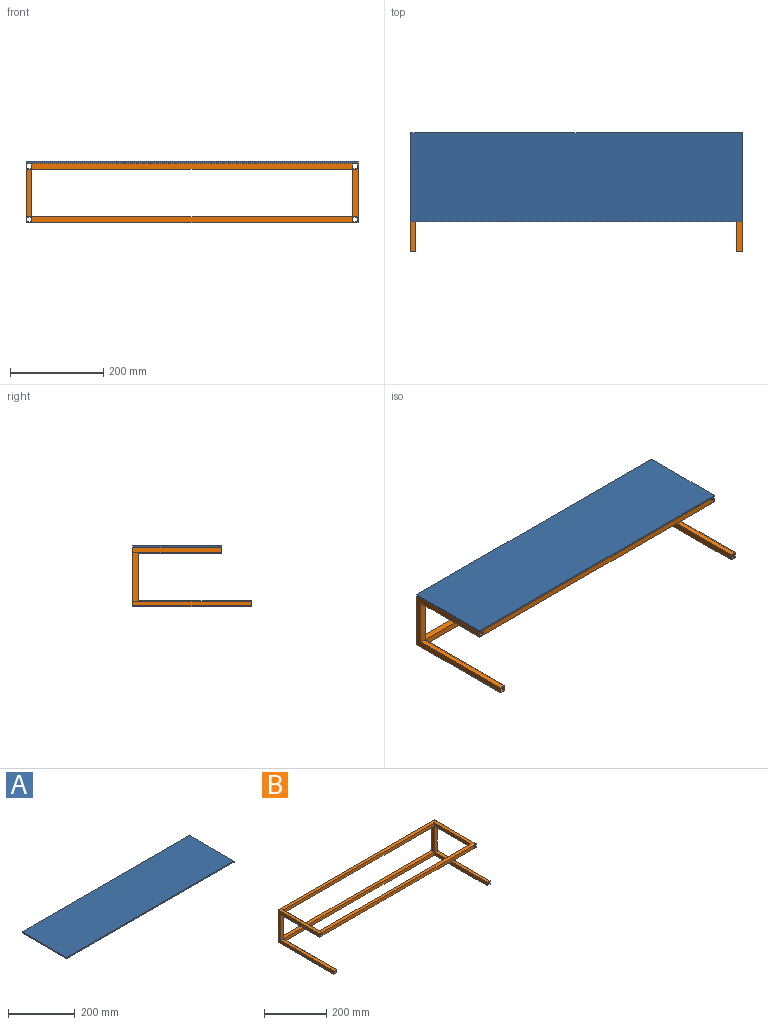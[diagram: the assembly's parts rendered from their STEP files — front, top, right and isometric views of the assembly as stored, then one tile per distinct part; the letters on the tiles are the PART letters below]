
ASSEMBLY  parts=2 mates=1
PART A: 6 faces, bbox 711.2x190.5x4.1 mm
  f0: plane 190.5x4.06mm, normal (-1,0,0), area 774.2mm2, adj f1,f3,f4,f5
  f1: plane 711.2x4.06mm, normal (0,-1,0), area 2890.3mm2, adj f0,f2,f4,f5
  f2: plane 190.5x4.06mm, normal (1,0,0), area 774.2mm2, adj f1,f3,f4,f5
  f3: plane 711.2x4.06mm, normal (0,1,0), area 2890.3mm2, adj f0,f2,f4,f5
  f4: plane 711.2x190.5mm, normal (0,0,1), area 135483.6mm2, adj f0,f1,f2,f3
  f5: plane 711.2x190.5mm, normal (0,0,-1), area 135483.6mm2, adj f0,f1,f2,f3
PART B: 40 faces, bbox 711.2x254x127 mm
  f0: plane 711.2x127mm, normal (0,1,0), area 20232.2mm2, adj f6,f7,f10,f11,f15,f17,f18,f22
  f1: plane 12.7x12.7mm, normal (0,-1,0), area 58.1mm2, adj f11,f12,f16,f17,f36,f37,f38,f39
  f2: plane 711.2x12.7mm, normal (0,-1,0), area 8825.8mm2, adj f11,f15,f18,f20,f28,f29,f30,f31
  f3: plane 12.7x12.7mm, normal (0,-1,0), area 58.1mm2, adj f9,f14,f15,f17,f24,f25,f26,f27
  f4: plane 165.1x12.7mm, normal (1,0,0), area 2096.8mm2, adj f18,f20,f21,f23
  f5: plane 165.1x12.7mm, normal (-1,0,0), area 2096.8mm2, adj f18,f20,f21,f23
  f6: plane 101.6x12.7mm, normal (1,0,0), area 1290.3mm2, adj f0,f8,f10,f22
  f7: plane 101.6x12.7mm, normal (-1,0,0), area 1290.3mm2, adj f0,f10,f19,f22
  f8: plane 101.6x12.7mm, normal (0,-1,0), area 1290.3mm2, adj f6,f11,f16,f20
  f9: plane 241.3x12.7mm, normal (0,0,1), area 3064.5mm2, adj f3,f14,f15,f19
  f10: plane 685.8x12.7mm, normal (0,0,1), area 8709.7mm2, adj f0,f6,f7,f13
  f11: plane 254x127mm, normal (-1,0,0), area 6935.5mm2, adj f0,f1,f2,f8,f16,f17,f18,f20
  f12: plane 241.3x12.7mm, normal (1,0,0), area 3064.5mm2, adj f1,f13,f16,f17
  f13: plane 685.8x12.7mm, normal (0,-1,0), area 8709.7mm2, adj f10,f12,f14,f17
  f14: plane 241.3x12.7mm, normal (-1,0,0), area 3064.5mm2, adj f3,f9,f13,f17
  f15: plane 254x127mm, normal (1,0,0), area 6935.5mm2, adj f0,f2,f3,f9,f17,f18,f19,f20
  f16: plane 241.3x12.7mm, normal (0,0,1), area 3064.5mm2, adj f1,f8,f11,f12
  f17: plane 711.2x254mm, normal (0,0,-1), area 15161.3mm2, adj f0,f1,f3,f11,f12,f13,f14,f15
  f18: plane 711.2x190.5mm, normal (0,0,1), area 22258mm2, adj f0,f2,f4,f5,f11,f15,f21,f23
  f19: plane 101.6x12.7mm, normal (0,-1,0), area 1290.3mm2, adj f7,f9,f15,f20
  f20: plane 711.2x177.8mm, normal (0,0,-1), area 13225.8mm2, adj f2,f4,f5,f8,f11,f15,f19,f23
  f21: plane 685.8x12.7mm, normal (0,-1,0), area 8709.7mm2, adj f4,f5,f18,f22
  f22: plane 685.8x12.7mm, normal (0,0,-1), area 8709.7mm2, adj f0,f6,f7,f21
  f23: plane 685.8x12.7mm, normal (0,1,0), area 8709.7mm2, adj f4,f5,f18,f20
  f24: plane 254x10.16mm, normal (0,0,-1), area 2580.6mm2, adj f0,f3,f25,f27
  f25: plane 254x10.16mm, normal (1,0,0), area 2580.6mm2, adj f0,f3,f24,f26
  f26: plane 254x10.16mm, normal (0,0,1), area 2580.6mm2, adj f0,f3,f25,f27
  f27: plane 254x10.16mm, normal (-1,0,0), area 2580.6mm2, adj f0,f3,f24,f26
  f28: plane 190.5x10.16mm, normal (0,0,-1), area 1935.5mm2, adj f0,f2,f29,f31
  f29: plane 190.5x10.16mm, normal (1,0,0), area 1935.5mm2, adj f0,f2,f28,f30
  f30: plane 190.5x10.16mm, normal (0,0,1), area 1935.5mm2, adj f0,f2,f29,f31
  f31: plane 190.5x10.16mm, normal (-1,0,0), area 1935.5mm2, adj f0,f2,f28,f30
  f32: plane 190.5x10.16mm, normal (-1,0,0), area 1935.5mm2, adj f0,f2,f33,f35
  f33: plane 190.5x10.16mm, normal (0,0,-1), area 1935.5mm2, adj f0,f2,f32,f34
  f34: plane 190.5x10.16mm, normal (1,0,0), area 1935.5mm2, adj f0,f2,f33,f35
  f35: plane 190.5x10.16mm, normal (0,0,1), area 1935.5mm2, adj f0,f2,f32,f34
  f36: plane 254x10.16mm, normal (0,0,-1), area 2580.6mm2, adj f0,f1,f37,f39
  f37: plane 254x10.16mm, normal (1,0,0), area 2580.6mm2, adj f0,f1,f36,f38
  f38: plane 254x10.16mm, normal (0,0,1), area 2580.6mm2, adj f0,f1,f37,f39
  f39: plane 254x10.16mm, normal (-1,0,0), area 2580.6mm2, adj f0,f1,f36,f38
PLACE A t=(-308.21,-100.47,-50.89)mm
PLACE B t=(-308.21,-163.97,-177.89)mm
MATE fastened B.f15 <-> A.f2  axis (1,0,0) through (402.99,-100.47,-50.89)mm
